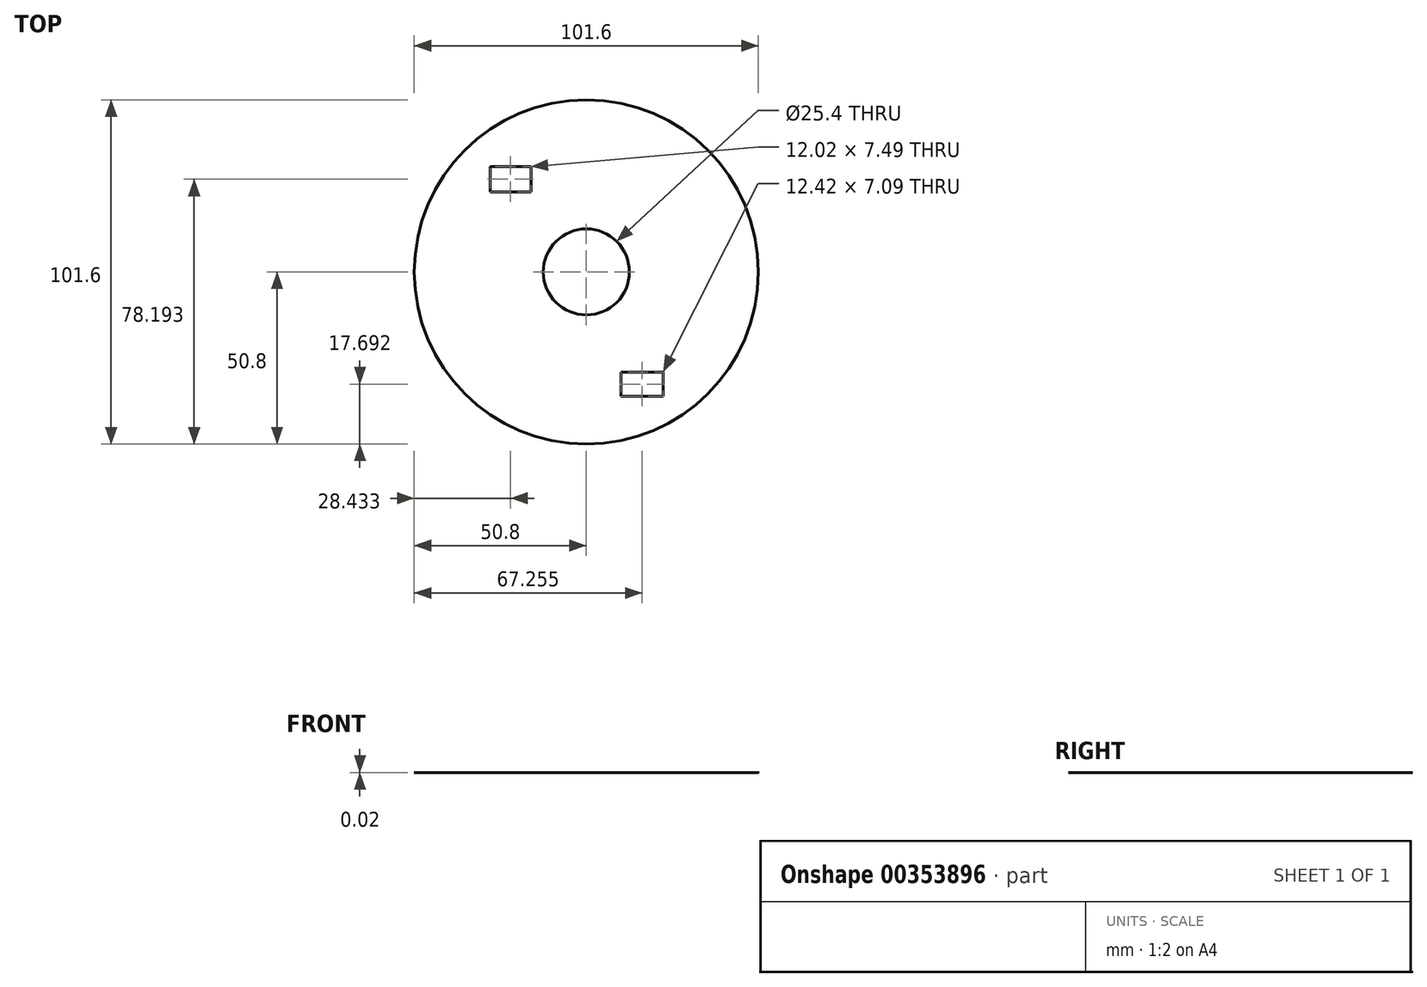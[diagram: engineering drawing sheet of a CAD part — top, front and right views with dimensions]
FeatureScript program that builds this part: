
annotation { "Feature Type Name" : "Feature", "Feature Type Description" : "" }
export const myFeature = defineFeature(function(context is Context, id is Id, definition is map)
    precondition{}
    {
        {
            var Q0;
            Q0=qCreatedBy(makeId("Top.planeOp"),FACE);
            var sketch = newSketch(context, id + "F0", { "sketchPlane" : qUnion([Q0])});
            skCircle(sketch, "E0", {"center": v(0, 0) * mm, "radius": 12.7 * mm});
            skCircle(sketch, "E1", {"center": v(0, 0) * mm, "radius": 50.8 * mm});
            skLineSegment(sketch, "E2.bottom", {"start": v(-28.38, 31.14) * mm, "end": v(-16.36, 31.14) * mm});
            skLineSegment(sketch, "E2.top", {"start": v(-28.38, 23.65) * mm, "end": v(-16.36, 23.65) * mm});
            skLineSegment(sketch, "E2.left", {"start": v(-28.38, 31.14) * mm, "end": v(-28.38, 23.65) * mm});
            skLineSegment(sketch, "E2.right", {"start": v(-16.36, 31.14) * mm, "end": v(-16.36, 23.65) * mm});
            skLineSegment(sketch, "E3.bottom", {"start": v(10.25, -29.56) * mm, "end": v(22.66, -29.56) * mm});
            skLineSegment(sketch, "E3.top", {"start": v(10.25, -36.65) * mm, "end": v(22.66, -36.65) * mm});
            skLineSegment(sketch, "E3.left", {"start": v(10.25, -29.56) * mm, "end": v(10.25, -36.65) * mm});
            skLineSegment(sketch, "E3.right", {"start": v(22.66, -29.56) * mm, "end": v(22.66, -36.65) * mm});
            skSolve(sketch);
        }
        {
            var Q0;
            Q0=makeQuery(id+"F0.imprint","IMPRINT",FACE,{"disambiguationData":[TD([[makeQuery(id+"F0.imprint","IMPRINT",EDGE,{"derivedFrom":sQuery(id+"F0.wireOp",EDGE,"E0")}),-1.0]])]});
            extrude(context, id + "F1", {"entities" : qUnion([Q0]), "endBound" : BoundingType.SYMMETRIC, "depth" : 1 / 50.8 * mm});
        }
    });
